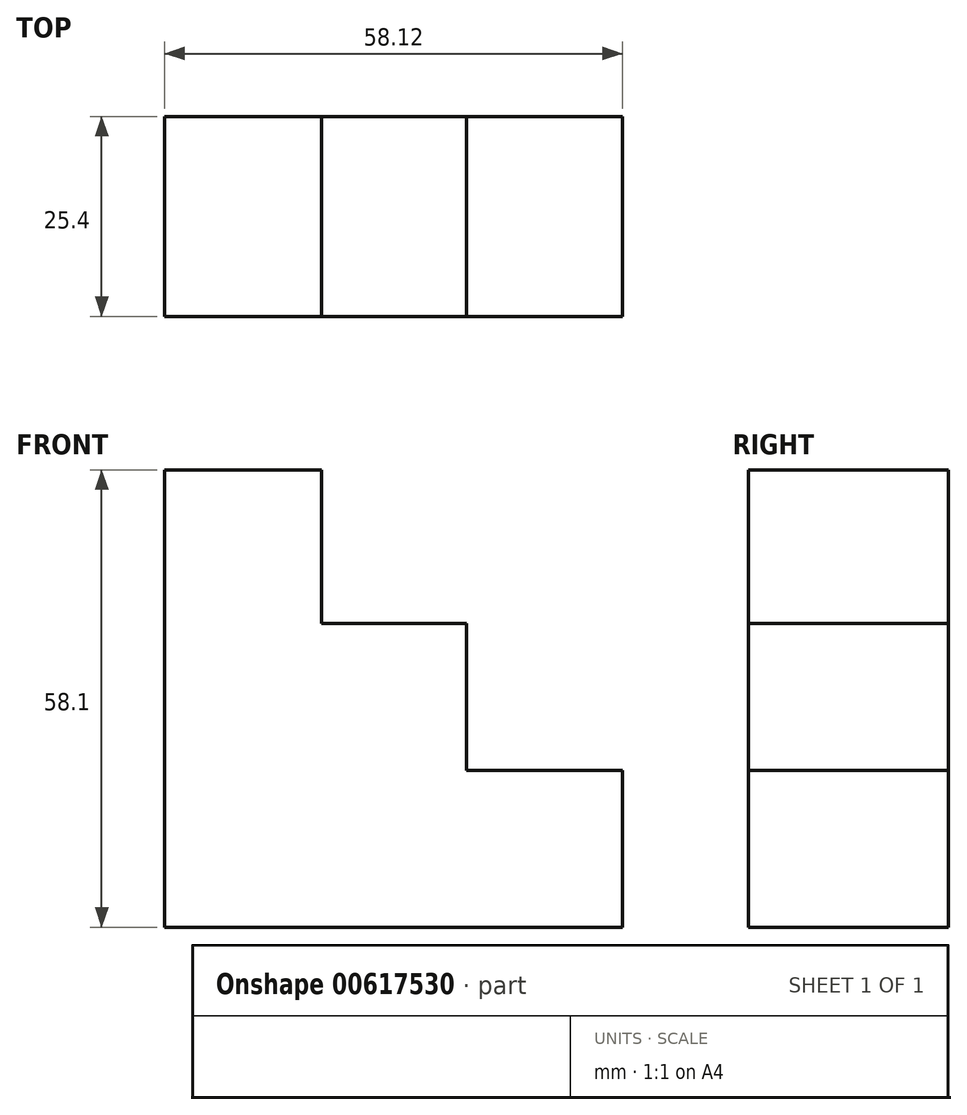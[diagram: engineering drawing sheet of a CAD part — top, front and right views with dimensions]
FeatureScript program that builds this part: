
annotation { "Feature Type Name" : "Feature", "Feature Type Description" : "" }
export const myFeature = defineFeature(function(context is Context, id is Id, definition is map)
    precondition{}
    {
        {
            var Q0;
            Q0=qCreatedBy(makeId("Front.planeOp"),FACE);
            var sketch = newSketch(context, id + "F0", { "sketchPlane" : qUnion([Q0])});
            skLineSegment(sketch, "E0", {"start": v(0, 0) * mm, "end": v(58.12, 0) * mm});
            skLineSegment(sketch, "E1", {"start": v(58.12, 0) * mm, "end": v(58.12, 19.9) * mm});
            skLineSegment(sketch, "E2", {"start": v(58.12, 19.9) * mm, "end": v(38.34, 19.9) * mm});
            skLineSegment(sketch, "E3", {"start": v(38.34, 19.9) * mm, "end": v(38.34, 38.55) * mm});
            skLineSegment(sketch, "E4", {"start": v(38.34, 38.55) * mm, "end": v(19.94, 38.55) * mm});
            skLineSegment(sketch, "E5", {"start": v(19.94, 38.55) * mm, "end": v(19.94, 58.1) * mm});
            skLineSegment(sketch, "E6", {"start": v(19.94, 58.1) * mm, "end": v(0, 58.1) * mm});
            skLineSegment(sketch, "E7", {"start": v(0, 58.1) * mm, "end": v(0, 0) * mm});
            skSolve(sketch);
        }
        {
            var Q0;
            Q0 = qSketchRegion(id + "F0", true);
            extrude(context, id + "F1", {"entities" : qUnion([Q0]), "depth" : 25.4 * mm, "offsetDistance" : 25.4 * mm});
        }
    });
